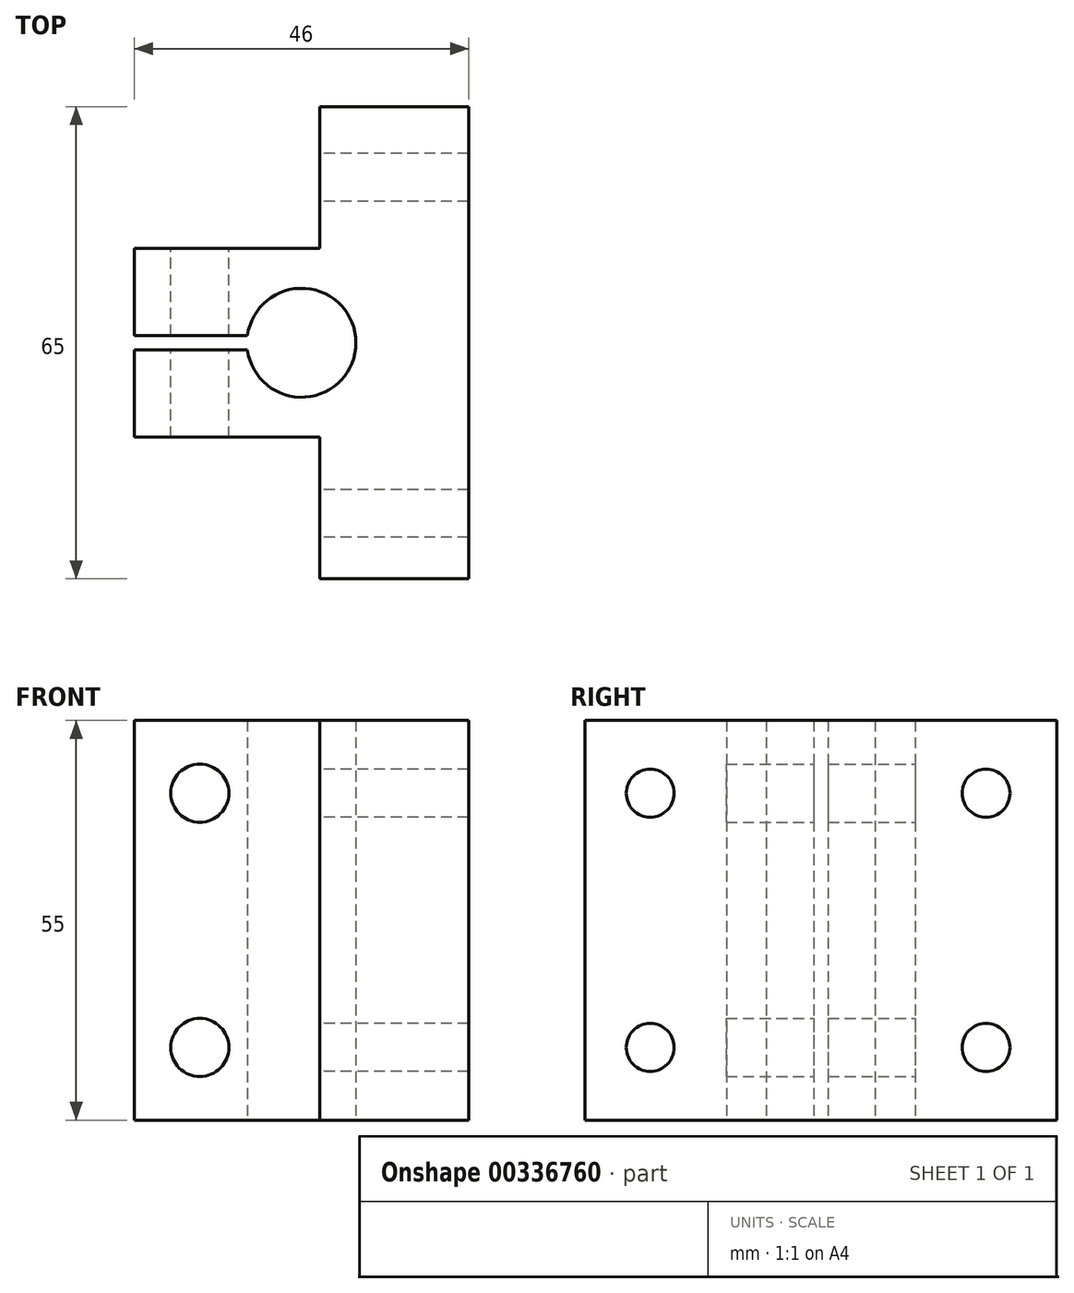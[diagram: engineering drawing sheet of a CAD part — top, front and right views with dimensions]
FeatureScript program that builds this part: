
annotation { "Feature Type Name" : "Feature", "Feature Type Description" : "" }
export const myFeature = defineFeature(function(context is Context, id is Id, definition is map)
    precondition{}
    {
        {
            var Q0;
            Q0=qCreatedBy(makeId("Top.planeOp"),FACE);
            var sketch = newSketch(context, id + "F0", { "sketchPlane" : qUnion([Q0])});
            skLineSegment(sketch, "E0", {"start": v(58.6, 55.99) * mm, "end": v(58.6, -9.01) * mm});
            skLineSegment(sketch, "E1", {"start": v(58.6, 55.99) * mm, "end": v(38.1, 55.99) * mm});
            skLineSegment(sketch, "E2", {"start": v(38.1, 55.99) * mm, "end": v(38.1, 36.49) * mm});
            skLineSegment(sketch, "E3", {"start": v(38.1, 36.49) * mm, "end": v(12.6, 36.49) * mm});
            skLineSegment(sketch, "E4", {"start": v(58.6, -9.01) * mm, "end": v(38.1, -9.01) * mm});
            skLineSegment(sketch, "E5", {"start": v(38.1, -9.01) * mm, "end": v(38.1, 10.49) * mm});
            skLineSegment(sketch, "E6", {"start": v(38.1, 10.49) * mm, "end": v(12.6, 10.49) * mm});
            skLineSegment(sketch, "E7", {"start": v(12.6, 10.49) * mm, "end": v(12.6, 22.49) * mm});
            skLineSegment(sketch, "E8", {"start": v(12.6, 36.49) * mm, "end": v(12.6, 24.49) * mm});
            skLineSegment(sketch, "E9", {"start": v(12.6, 24.49) * mm, "end": v(28.16, 24.49) * mm});
            skLineSegment(sketch, "E10", {"start": v(12.6, 22.49) * mm, "end": v(28.16, 22.49) * mm});
            skArc(sketch, "E11", {"start": v(28.16, 22.49) * mm, "mid": v(43.1, 23.49) * mm, "end": v(28.16, 24.49) * mm});
            skPoint(sketch, "E12.orphan", {"position": v(35.6, 22.49) * mm});
            skPoint(sketch, "E13.end.orphan", {"position": v(35.6, 24.49) * mm});
            skSolve(sketch);
        }
        {
            var Q0;
            Q0 = qSketchRegion(id + "F0", true);
            extrude(context, id + "F1", {"entities" : qUnion([Q0]), "depth" : 55 * mm});
        }
        {
            var Q0;
            Q0=makeQuery(id+"F1.opExtrude","SWEPT_FACE",FACE,{"disambiguationData":[OSD([sQuery(id+"F0.wireOp",EDGE,"E3")])]});
            var sketch = newSketch(context, id + "F2", { "sketchPlane" : qUnion([Q0])});
            skLineSegment(sketch, "E14", {"start": v(-12.6, 0) * mm, "end": v(-12.6, 10) * mm});
            skLineSegment(sketch, "E15", {"start": v(-12.6, 10) * mm, "end": v(-21.6, 10) * mm});
            skLineSegment(sketch, "E16", {"start": v(-21.6, 55) * mm, "end": v(-21.6, 45) * mm});
            skCircle(sketch, "E17", {"center": v(-21.6, 10) * mm, "radius": 4 * mm});
            skCircle(sketch, "E18", {"center": v(-21.6, 45) * mm, "radius": 4 * mm});
            skSolve(sketch);
        }
        {
            var Q0;
            Q0=makeQuery(id+"F2.imprint","IMPRINT",FACE,{"disambiguationData":[TD([[makeQuery(id+"F2.imprint","IMPRINT",EDGE,{"derivedFrom":sQuery(id+"F2.wireOp",EDGE,"E17")}),1.0]])]});
            var Q1;
            Q1=makeQuery(id+"F2.imprint","IMPRINT",FACE,{"disambiguationData":[TD([[makeQuery(id+"F2.imprint","IMPRINT",EDGE,{"derivedFrom":sQuery(id+"F2.wireOp",EDGE,"E18")}),1.0]])]});
            extrude(context, id + "F3", {"entities" : qUnion([Q0, Q1]), "operationType" : NewBodyOperationType.REMOVE, "oppositeDirection" : true, "depth" : 29.3 * mm});
        }
        {
            var Q0;
            Q0=makeQuery(id+"F1.opExtrude","SWEPT_FACE",FACE,{"disambiguationData":[OSD([sQuery(id+"F0.wireOp",EDGE,"E5")])]});
            var sketch = newSketch(context, id + "F4", { "sketchPlane" : qUnion([Q0])});
            skLineSegment(sketch, "E19", {"start": v(0, 55) * mm, "end": v(0, 45) * mm});
            skCircle(sketch, "E20", {"center": v(0, 45) * mm, "radius": 3.3 * mm});
            skLineSegment(sketch, "E21", {"start": v(0, 0) * mm, "end": v(0, 10) * mm});
            skCircle(sketch, "E22", {"center": v(0, 10) * mm, "radius": 3.3 * mm});
            skSolve(sketch);
        }
        {
            var Q0;
            Q0=makeQuery(id+"F4.imprint","IMPRINT",FACE,{"disambiguationData":[TD([[makeQuery(id+"F4.imprint","IMPRINT",EDGE,{"derivedFrom":sQuery(id+"F4.wireOp",EDGE,"E20")}),1.0]])]});
            var Q1;
            Q1=makeQuery(id+"F4.imprint","IMPRINT",FACE,{"disambiguationData":[TD([[makeQuery(id+"F4.imprint","IMPRINT",EDGE,{"derivedFrom":sQuery(id+"F4.wireOp",EDGE,"E22")}),1.0]])]});
            extrude(context, id + "F5", {"entities" : qUnion([Q0, Q1]), "operationType" : NewBodyOperationType.REMOVE, "oppositeDirection" : true, "depth" : 33.2 * mm});
        }
        {
            var Q0;
            Q0=makeQuery(id+"F1.opExtrude","SWEPT_FACE",FACE,{"disambiguationData":[OSD([sQuery(id+"F0.wireOp",EDGE,"E2")])]});
            var sketch = newSketch(context, id + "F6", { "sketchPlane" : qUnion([Q0])});
            skLineSegment(sketch, "E23", {"start": v(-46.24, 0) * mm, "end": v(-46.24, 10) * mm});
            skLineSegment(sketch, "E24", {"start": v(-46.24, 55) * mm, "end": v(-46.24, 45) * mm});
            skPoint(sketch, "E24.endSnap0", {"position": v(-46.24, 55) * mm});
            skCircle(sketch, "E25", {"center": v(-46.24, 45) * mm, "radius": 3.3 * mm});
            skCircle(sketch, "E26", {"center": v(-46.24, 10) * mm, "radius": 3.3 * mm});
            skSolve(sketch);
        }
        {
            var Q0;
            Q0=makeQuery(id+"F6.imprint","IMPRINT",FACE,{"disambiguationData":[TD([[makeQuery(id+"F6.imprint","IMPRINT",EDGE,{"derivedFrom":sQuery(id+"F6.wireOp",EDGE,"E25")}),1.0]])]});
            extrude(context, id + "F7", {"entities" : qUnion([Q0]), "operationType" : NewBodyOperationType.REMOVE, "oppositeDirection" : true, "depth" : 34.5 * mm});
        }
        {
            var Q0;
            Q0=makeQuery(id+"F1.opExtrude","SWEPT_FACE",FACE,{"disambiguationData":[OSD([sQuery(id+"F0.wireOp",EDGE,"E2")])]});
            var sketch = newSketch(context, id + "F8", { "sketchPlane" : qUnion([Q0])});
            skLineSegment(sketch, "E27", {"start": v(-46.24, 0) * mm, "end": v(-46.24, 10) * mm});
            skCircle(sketch, "E28", {"center": v(-46.24, 10) * mm, "radius": 3.3 * mm});
            skSolve(sketch);
        }
        {
            var Q0;
            Q0=makeQuery(id+"F8.imprint","IMPRINT",FACE,{"disambiguationData":[TD([[makeQuery(id+"F8.imprint","IMPRINT",EDGE,{"derivedFrom":sQuery(id+"F8.wireOp",EDGE,"E28")}),1.0]])]});
            extrude(context, id + "F9", {"entities" : qUnion([Q0]), "operationType" : NewBodyOperationType.REMOVE, "oppositeDirection" : true, "depth" : 37.2 * mm});
        }
    });
